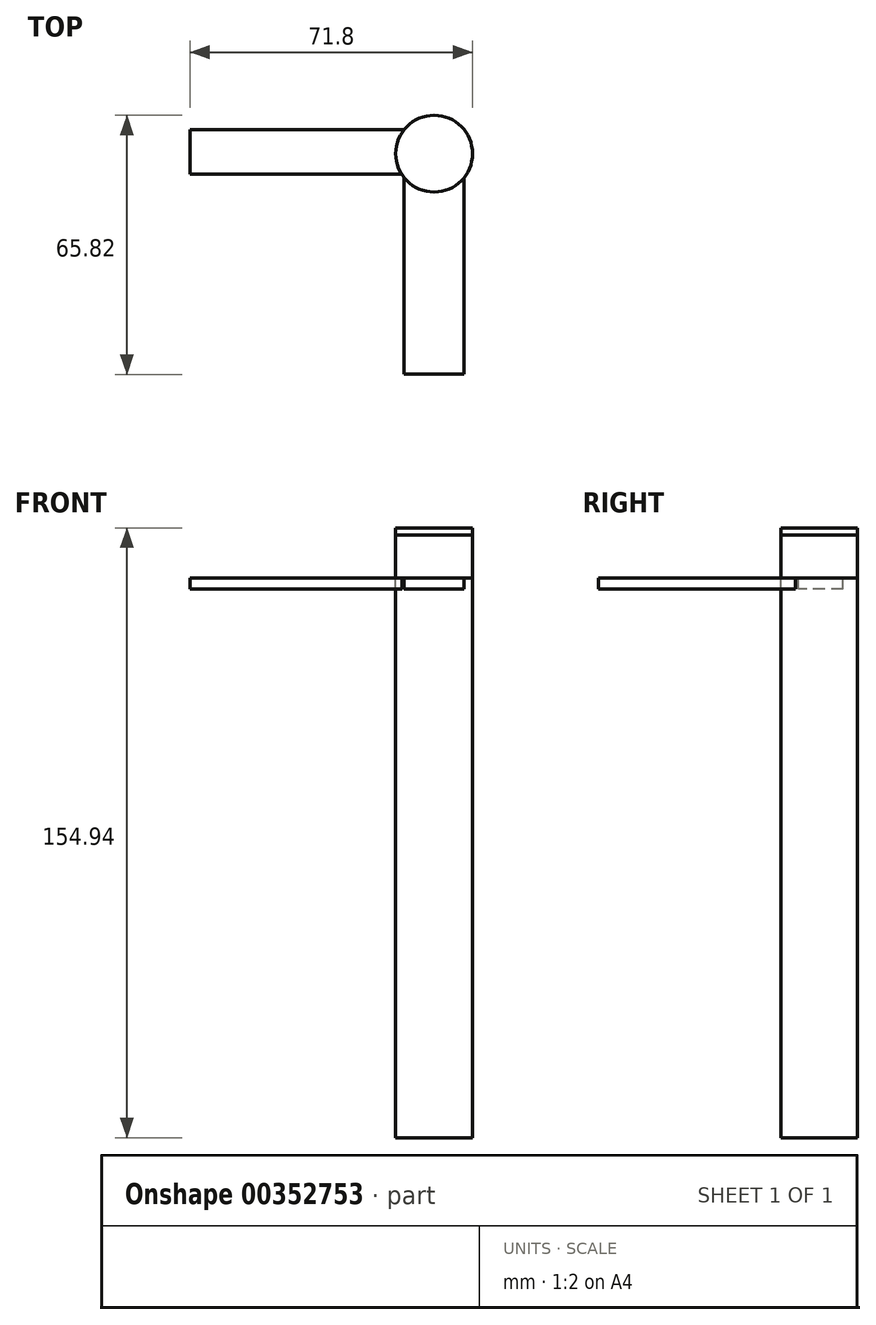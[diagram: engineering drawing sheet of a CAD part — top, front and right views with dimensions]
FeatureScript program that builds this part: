
annotation { "Feature Type Name" : "Feature", "Feature Type Description" : "" }
export const myFeature = defineFeature(function(context is Context, id is Id, definition is map)
    precondition{}
    {
        {
            var Q0;
            Q0=qCreatedBy(makeId("Top.planeOp"),FACE);
            var sketch = newSketch(context, id + "F0", { "sketchPlane" : qUnion([Q0])});
            skCircle(sketch, "E0", {"center": v(0, 0) * mm, "radius": 9.75 * mm});
            skLineSegment(sketch, "E1.bottom", {"start": v(7.63, 6.07) * mm, "end": v(62.05, 6.07) * mm});
            skLineSegment(sketch, "E1.top", {"start": v(7.63, -5.26) * mm, "end": v(62.05, -5.26) * mm});
            skLineSegment(sketch, "E1.left", {"start": v(7.63, 6.07) * mm, "end": v(7.63, -5.26) * mm});
            skLineSegment(sketch, "E1.right", {"start": v(62.05, 6.07) * mm, "end": v(62.05, -5.26) * mm});
            skLineSegment(sketch, "E2.MirrorCS", {"start": v(-7.63, 6.07) * mm, "end": v(-7.63, -5.26) * mm});
            skLineSegment(sketch, "E3.MirrorCS", {"start": v(-62.05, 6.07) * mm, "end": v(-62.05, -5.26) * mm});
            skLineSegment(sketch, "E4.MirrorCS", {"start": v(-7.63, 6.07) * mm, "end": v(-62.05, 6.07) * mm});
            skLineSegment(sketch, "E5.MirrorCS", {"start": v(-7.63, -5.26) * mm, "end": v(-62.05, -5.26) * mm});
            skPoint(sketch, "E6.oppositeSnap0", {"position": v(7.63, 0.4) * mm});
            skLineSegment(sketch, "E6.bottom", {"start": v(-7.63, 6.07) * mm, "end": v(7.63, 6.07) * mm});
            skLineSegment(sketch, "E6.top", {"start": v(-7.63, 56.07) * mm, "end": v(7.63, 56.07) * mm});
            skLineSegment(sketch, "E6.left", {"start": v(-7.63, 6.07) * mm, "end": v(-7.63, 56.07) * mm});
            skLineSegment(sketch, "E6.right", {"start": v(7.63, 6.07) * mm, "end": v(7.63, 56.07) * mm});
            skLineSegment(sketch, "E7.MirrorCS", {"start": v(-7.63, -56.07) * mm, "end": v(7.63, -56.07) * mm});
            skLineSegment(sketch, "E8.MirrorCS", {"start": v(-7.63, -6.07) * mm, "end": v(7.63, -6.07) * mm});
            skLineSegment(sketch, "E9.MirrorCS", {"start": v(-7.63, -6.07) * mm, "end": v(-7.63, -56.07) * mm});
            skLineSegment(sketch, "E10.MirrorCS", {"start": v(7.63, -6.07) * mm, "end": v(7.63, -56.07) * mm});
            skSolve(sketch);
        }
        {
            var Q0;
            {var subQ0=sQuery(id+"F0.wireOp",EDGE,"E1.left");Q0=makeQuery(id+"F0.imprint","IMPRINT",FACE,{"disambiguationData":[TD([[makeQuery(id+"F0.imprint","IMPRINT",EDGE,{"derivedFrom":subQ0}),-1.0]])]});}
            var Q1;
            {var subQ0=sQuery(id+"F0.wireOp",EDGE,"E6.bottom");Q1=makeQuery(id+"F0.imprint","IMPRINT",FACE,{"disambiguationData":[TD([[makeQuery(id+"F0.imprint","IMPRINT",EDGE,{"derivedFrom":subQ0}),1.0]])]});}
            var Q2;
            {var subQ0=sQuery(id+"F0.wireOp",EDGE,"E2.MirrorCS");Q2=makeQuery(id+"F0.imprint","IMPRINT",FACE,{"disambiguationData":[TD([[makeQuery(id+"F0.imprint","IMPRINT",EDGE,{"derivedFrom":subQ0}),-1.0]])]});}
            var Q3;
            {var subQ0=sQuery(id+"F0.wireOp",EDGE,"E8.MirrorCS");Q3=makeQuery(id+"F0.imprint","IMPRINT",FACE,{"disambiguationData":[TD([[makeQuery(id+"F0.imprint","IMPRINT",EDGE,{"derivedFrom":subQ0}),-1.0]])]});}
            var Q4;
            {var subQ0=sQuery(id+"F0.wireOp",EDGE,"E1.left");Q4=makeQuery(id+"F0.imprint","IMPRINT",FACE,{"disambiguationData":[TD([[makeQuery(id+"F0.imprint","IMPRINT",EDGE,{"derivedFrom":subQ0}),1.0]])]});}
            extrude(context, id + "F1", {"entities" : qUnion([Q0, Q1, Q2, Q3, Q4]), "depth" : 10.92 * mm});
        }
        {
            var Q0;
            Q0=makeQuery(id+"F0.imprint","IMPRINT",FACE,{"disambiguationData":[TD([[makeQuery(id+"F0.imprint","IMPRINT",EDGE,{"derivedFrom":sQuery(id+"F0.wireOp",EDGE,"E7.MirrorCS")}),1.0]])]});
            var Q1;
            {var subQ4=sQuery(id+"F0.wireOp",EDGE,"E3.MirrorCS");Q1=makeQuery(id+"F0.imprint","IMPRINT",FACE,{"disambiguationData":[TD([[makeQuery(id+"F0.imprint","IMPRINT",EDGE,{"derivedFrom":subQ4}),1.0]])]});}
            extrude(context, id + "F2", {"entities" : qUnion([Q0, Q1]), "oppositeDirection" : true, "depth" : 2.8 * mm});
        }
        {
            var Q0;
            {var subQ0=sQuery(id+"F0.wireOp",EDGE,"E1.left");Q0=makeQuery(id+"F0.imprint","IMPRINT",FACE,{"disambiguationData":[TD([[makeQuery(id+"F0.imprint","IMPRINT",EDGE,{"derivedFrom":subQ0}),-1.0]])]});}
            var Q1;
            {var subQ0=sQuery(id+"F0.wireOp",EDGE,"E8.MirrorCS");Q1=makeQuery(id+"F0.imprint","IMPRINT",FACE,{"disambiguationData":[TD([[makeQuery(id+"F0.imprint","IMPRINT",EDGE,{"derivedFrom":subQ0}),-1.0]])]});}
            var Q2;
            {var subQ0=sQuery(id+"F0.wireOp",EDGE,"E6.bottom");Q2=makeQuery(id+"F0.imprint","IMPRINT",FACE,{"disambiguationData":[TD([[makeQuery(id+"F0.imprint","IMPRINT",EDGE,{"derivedFrom":subQ0}),1.0]])]});}
            var Q3;
            {var subQ0=sQuery(id+"F0.wireOp",EDGE,"E2.MirrorCS");Q3=makeQuery(id+"F0.imprint","IMPRINT",FACE,{"disambiguationData":[TD([[makeQuery(id+"F0.imprint","IMPRINT",EDGE,{"derivedFrom":subQ0}),-1.0]])]});}
            var Q4;
            {var subQ0=sQuery(id+"F0.wireOp",EDGE,"E1.left");Q4=makeQuery(id+"F0.imprint","IMPRINT",FACE,{"disambiguationData":[TD([[makeQuery(id+"F0.imprint","IMPRINT",EDGE,{"derivedFrom":subQ0}),1.0]])]});}
            extrude(context, id + "F3", {"entities" : qUnion([Q0, Q1, Q2, Q3, Q4]), "depth" : 12.7 * mm, "hasSecondDirection" : true, "secondDirectionOppositeDirection" : true, "secondDirectionDepth" : 142.24 * mm});
        }
    });
